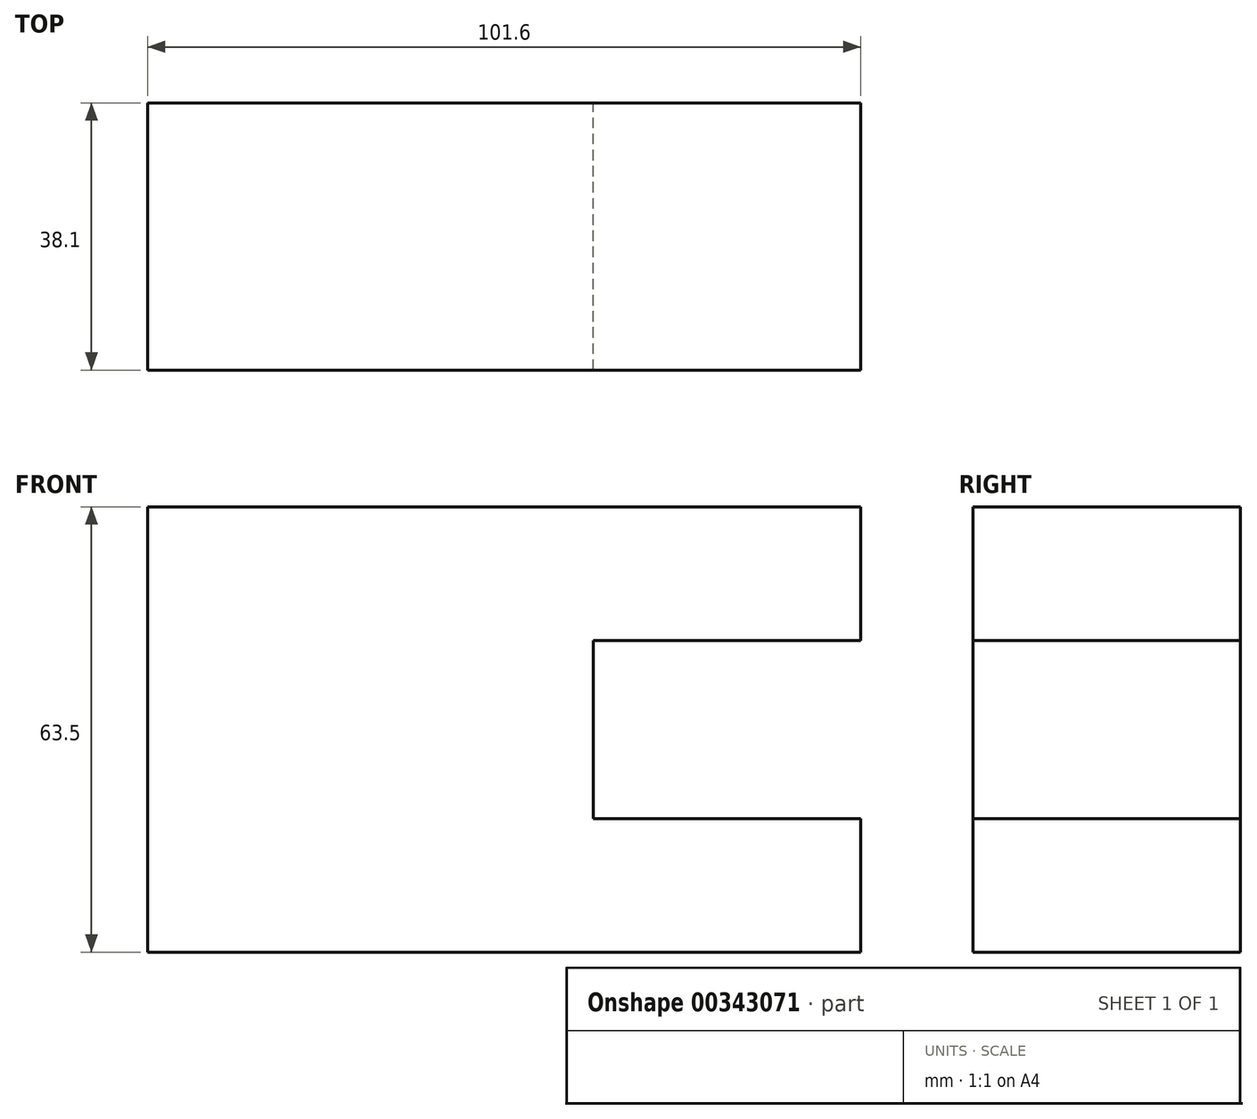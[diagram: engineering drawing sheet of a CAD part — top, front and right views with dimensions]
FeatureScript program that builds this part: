
annotation { "Feature Type Name" : "Feature", "Feature Type Description" : "" }
export const myFeature = defineFeature(function(context is Context, id is Id, definition is map)
    precondition{}
    {
        {
            var Q0;
            Q0=qCreatedBy(makeId("Front.planeOp"),FACE);
            var sketch = newSketch(context, id + "F0", { "sketchPlane" : qUnion([Q0])});
            skLineSegment(sketch, "E0", {"start": v(-45.76, -36.29) * mm, "end": v(55.84, -36.29) * mm});
            skLineSegment(sketch, "E1", {"start": v(55.84, -36.29) * mm, "end": v(55.84, -17.24) * mm});
            skLineSegment(sketch, "E2", {"start": v(55.84, -17.24) * mm, "end": v(17.74, -17.24) * mm});
            skLineSegment(sketch, "E3", {"start": v(-45.76, -36.29) * mm, "end": v(-45.76, 27.21) * mm});
            skLineSegment(sketch, "E4", {"start": v(-45.76, 27.21) * mm, "end": v(55.84, 27.21) * mm});
            skLineSegment(sketch, "E5", {"start": v(55.84, 27.21) * mm, "end": v(55.84, 8.16) * mm});
            skLineSegment(sketch, "E6", {"start": v(55.84, 8.16) * mm, "end": v(17.74, 8.16) * mm});
            skLineSegment(sketch, "E7", {"start": v(17.74, 8.16) * mm, "end": v(17.74, -17.24) * mm});
            skSolve(sketch);
        }
        {
            var Q0;
            Q0 = qSketchRegion(id + "F0", true);
            extrude(context, id + "F1", {"entities" : qUnion([Q0]), "depth" : 38.1 * mm});
        }
    });
